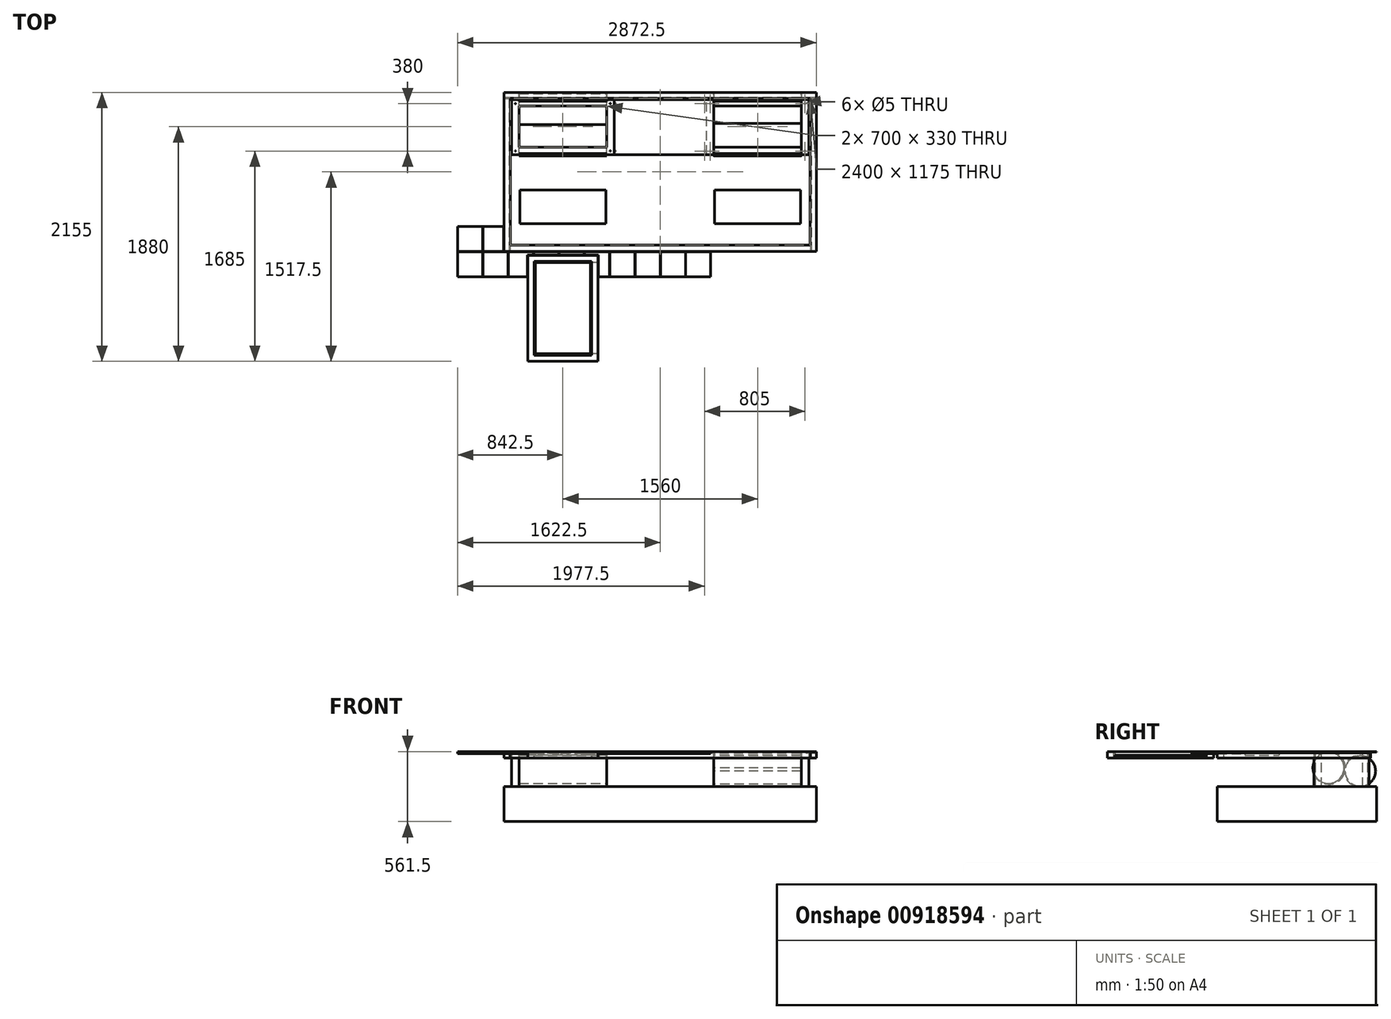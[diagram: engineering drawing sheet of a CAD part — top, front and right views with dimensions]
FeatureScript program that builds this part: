
annotation { "Feature Type Name" : "Feature", "Feature Type Description" : "" }
export const myFeature = defineFeature(function(context is Context, id is Id, definition is map)
    precondition{}
    {
        {
            var Q0;
            Q0=qCreatedBy(makeId("Top.planeOp"),FACE);
            var sketch = newSketch(context, id + "F0", { "sketchPlane" : qUnion([Q0])});
            skLineSegment(sketch, "E0.bottom", {"start": v(-1000, 0) * mm, "end": v(-560, 0) * mm});
            skLineSegment(sketch, "E0.top", {"start": v(-1000, 730) * mm, "end": v(-560, 730) * mm});
            skLineSegment(sketch, "E0.left", {"start": v(-1000, 0) * mm, "end": v(-1000, 730) * mm});
            skLineSegment(sketch, "E0.right", {"start": v(-560, 0) * mm, "end": v(-560, 730) * mm});
            skLineSegment(sketch, "E1.bottom", {"start": v(-1190, 880) * mm, "end": v(1190, 880) * mm});
            skLineSegment(sketch, "E1.top", {"start": v(-1190, 1475) * mm, "end": v(1190, 1475) * mm});
            skLineSegment(sketch, "E1.left", {"start": v(-1190, 880) * mm, "end": v(-1190, 1475) * mm});
            skLineSegment(sketch, "E1.right", {"start": v(1190, 880) * mm, "end": v(1190, 1475) * mm});
            skLineSegment(sketch, "E2.bottom", {"start": v(-1190, 1595) * mm, "end": v(1190, 1595) * mm});
            skLineSegment(sketch, "E2.top", {"start": v(-1190, 2035) * mm, "end": v(1190, 2035) * mm});
            skLineSegment(sketch, "E2.left", {"start": v(-1190, 1595) * mm, "end": v(-1190, 2035) * mm});
            skLineSegment(sketch, "E2.right", {"start": v(1190, 1595) * mm, "end": v(1190, 2035) * mm});
            skLineSegment(sketch, "E3", {"start": v(0, 0) * mm, "end": v(0, 2541.23) * mm, "construction": true});
            skLineSegment(sketch, "E4", {"start": v(-2590, 9087.14) * mm, "end": v(-2590, 297.64) * mm, "construction": true});
            skLineSegment(sketch, "E5", {"start": v(-3236.4, 5035) * mm, "end": v(-2134.23, 5035) * mm, "construction": true});
            skLineSegment(sketch, "E6", {"start": v(-3316.35, 8035) * mm, "end": v(-2134.23, 8035) * mm, "construction": true});
            skLineSegment(sketch, "E7.bottom", {"start": v(-1200, 2045) * mm, "end": v(1200, 2045) * mm});
            skLineSegment(sketch, "E7.top", {"start": v(-1200, 870) * mm, "end": v(1200, 870) * mm});
            skLineSegment(sketch, "E7.left", {"start": v(-1200, 2045) * mm, "end": v(-1200, 870) * mm});
            skLineSegment(sketch, "E7.right", {"start": v(1200, 2045) * mm, "end": v(1200, 870) * mm});
            skLineSegment(sketch, "E8.bottom", {"start": v(-1250, 2095) * mm, "end": v(1250, 2095) * mm});
            skLineSegment(sketch, "E8.top", {"start": v(-1250, 820) * mm, "end": v(1250, 820) * mm});
            skLineSegment(sketch, "E8.left", {"start": v(-1250, 2095) * mm, "end": v(-1250, 820) * mm});
            skLineSegment(sketch, "E8.right", {"start": v(1250, 2095) * mm, "end": v(1250, 820) * mm});
            skLineSegment(sketch, "E9", {"start": v(-780, -123.86) * mm, "end": v(-780, 1756.73) * mm, "construction": true});
            skPoint(sketch, "E9.startSnap0", {"position": v(-780, 0) * mm});
            skLineSegment(sketch, "E10.bottom", {"start": v(-1125, 1314) * mm, "end": v(-435, 1314) * mm});
            skLineSegment(sketch, "E10.top", {"start": v(-1125, 1041) * mm, "end": v(-435, 1041) * mm});
            skLineSegment(sketch, "E10.left", {"start": v(-1125, 1314) * mm, "end": v(-1125, 1041) * mm});
            skLineSegment(sketch, "E10.right", {"start": v(-435, 1314) * mm, "end": v(-435, 1041) * mm});
            skLineSegment(sketch, "E11.MirrorCS", {"start": v(1125, 1041) * mm, "end": v(435, 1041) * mm});
            skLineSegment(sketch, "E12.MirrorCS", {"start": v(435, 1314) * mm, "end": v(435, 1041) * mm});
            skLineSegment(sketch, "E13.MirrorCS", {"start": v(1125, 1314) * mm, "end": v(435, 1314) * mm});
            skLineSegment(sketch, "E14.MirrorCS", {"start": v(1125, 1314) * mm, "end": v(1125, 1041) * mm});
            skSolve(sketch);
        }
        {
            var Q0;
            Q0 = qSketchRegion(id + "F0", true);
            var Q1;
            Q1=makeQuery(id+"F0.imprint","IMPRINT",FACE,{"disambiguationData":[TD([[makeQuery(id+"F0.imprint","IMPRINT",EDGE,{"derivedFrom":sQuery(id+"F0.wireOp",EDGE,"E1.bottom")}),-1.0]])]});
            var Q2;
            Q2=makeQuery(id+"F0.imprint","IMPRINT",FACE,{"disambiguationData":[TD([[makeQuery(id+"F0.imprint","IMPRINT",EDGE,{"derivedFrom":sQuery(id+"F0.wireOp",EDGE,"E2.bottom")}),1.0]])]});
            var Q3;
            Q3=makeQuery(id+"F0.imprint","IMPRINT",FACE,{"disambiguationData":[TD([[makeQuery(id+"F0.imprint","IMPRINT",EDGE,{"derivedFrom":sQuery(id+"F0.wireOp",EDGE,"E10.bottom")}),-1.0]])]});
            var Q4;
            Q4=makeQuery(id+"F0.imprint","IMPRINT",FACE,{"disambiguationData":[TD([[makeQuery(id+"F0.imprint","IMPRINT",EDGE,{"derivedFrom":sQuery(id+"F0.wireOp",EDGE,"E1.bottom")}),1.0]])]});
            var Q5;
            Q5=makeQuery(id+"F0.imprint","IMPRINT",FACE,{"disambiguationData":[TD([[makeQuery(id+"F0.imprint","IMPRINT",EDGE,{"derivedFrom":sQuery(id+"F0.wireOp",EDGE,"E11.MirrorCS")}),-1.0]])]});
            extrude(context, id + "F1", {"entities" : qUnion([Q0, Q1, Q2, Q3, Q4, Q5]), "oppositeDirection" : true, "depth" : 280 * mm, "offsetDistance" : 25 * mm});
        }
        {
            var Q0;
            Q0=makeQuery(id+"F0.imprint","IMPRINT",FACE,{"disambiguationData":[TD([[makeQuery(id+"F0.imprint","IMPRINT",EDGE,{"derivedFrom":sQuery(id+"F0.wireOp",EDGE,"E2.bottom")}),1.0]])]});
            var Q1;
            Q1=makeQuery(id+"F0.imprint","IMPRINT",FACE,{"disambiguationData":[TD([[makeQuery(id+"F0.imprint","IMPRINT",EDGE,{"derivedFrom":sQuery(id+"F0.wireOp",EDGE,"E10.bottom")}),-1.0]])]});
            var Q2;
            Q2=makeQuery(id+"F0.imprint","IMPRINT",FACE,{"disambiguationData":[TD([[makeQuery(id+"F0.imprint","IMPRINT",EDGE,{"derivedFrom":sQuery(id+"F0.wireOp",EDGE,"E11.MirrorCS")}),-1.0]])]});
            var Q3;
            Q3=makeQuery(id+"F0.imprint","IMPRINT",FACE,{"disambiguationData":[TD([[makeQuery(id+"F0.imprint","IMPRINT",EDGE,{"derivedFrom":sQuery(id+"F0.wireOp",EDGE,"E0.bottom")}),1.0]])]});
            var Q4;
            Q4=makeQuery(id+"F0.imprint","IMPRINT",FACE,{"disambiguationData":[TD([[makeQuery(id+"F0.imprint","IMPRINT",EDGE,{"derivedFrom":sQuery(id+"F0.wireOp",EDGE,"E7.bottom")}),1.0]])]});
            extrude(context, id + "F2", {"entities" : qUnion([Q0, Q1, Q2, Q3, Q4]), "depth" : 280 * mm, "offsetDistance" : 25 * mm});
        }
        {
            var Q0;
            Q0=makeQuery(id+"F2.opExtrude","SWEPT_FACE",FACE,{"disambiguationData":[OSD([sQuery(id+"F0.wireOp",EDGE,"E8.top")])]});
            var sketch = newSketch(context, id + "F3", { "sketchPlane" : qUnion([Q0])});
            skLineSegment(sketch, "E15.0.0", {"start": v(-1250, 0) * mm, "end": v(1250, 0) * mm});
            skLineSegment(sketch, "E15.0.1", {"start": v(1250, 0) * mm, "end": v(1250, 280) * mm});
            skLineSegment(sketch, "E15.0.2", {"start": v(1250, 280) * mm, "end": v(-1250, 280) * mm});
            skLineSegment(sketch, "E15.0.3", {"start": v(-1250, 280) * mm, "end": v(-1250, 0) * mm});
            skLineSegment(sketch, "E16", {"start": v(-1204, 271) * mm, "end": v(-1204, 253.4) * mm});
            skLineSegment(sketch, "E17", {"start": v(-1204, 276) * mm, "end": v(-1203.5, 276) * mm});
            skLineSegment(sketch, "E18", {"start": v(-1200, 230) * mm, "end": v(-1200, 0) * mm});
            skLineSegment(sketch, "E19.bottom", {"start": v(-1200, 230) * mm, "end": v(1200, 230) * mm});
            skLineSegment(sketch, "E19.top", {"start": v(-1200, 0) * mm, "end": v(1200, 0) * mm});
            skLineSegment(sketch, "E19.right", {"start": v(1200, 230) * mm, "end": v(1200, 0) * mm});
            skPoint(sketch, "E20.visualSharp", {"position": v(-1204, 276) * mm});
            skArc(sketch, "E20.filletArc", {"start": v(-1204, 271) * mm, "mid": v(-1205.46, 274.54) * mm, "end": v(-1209, 276) * mm});
            skLineSegment(sketch, "E21", {"start": v(-1200, 230) * mm, "end": v(-1200, 280) * mm});
            skLineSegment(sketch, "E22.bottom", {"start": v(-1204, 271) * mm, "end": v(-1200, 271) * mm});
            skLineSegment(sketch, "E22.top", {"start": v(-1203.28, 230) * mm, "end": v(-1200, 230) * mm});
            skLineSegment(sketch, "E22.right", {"start": v(-1200, 271) * mm, "end": v(-1200, 230) * mm});
            skLineSegment(sketch, "E23", {"start": v(-1204, 271) * mm, "end": v(-1203.28, 230) * mm});
            skLineSegment(sketch, "E24", {"start": v(-1203.5, 276) * mm, "end": v(-1204, 276) * mm});
            skLineSegment(sketch, "E25", {"start": v(-1209, 276) * mm, "end": v(-1250, 276.72) * mm});
            skLineSegment(sketch, "E26.MirrorCS", {"start": v(-1209, -276) * mm, "end": v(-1250, -276.72) * mm});
            skLineSegment(sketch, "E27.MirrorCS", {"start": v(-1204, -271) * mm, "end": v(-1203.28, -230) * mm});
            skArc(sketch, "E28.MirrorCS", {"start": v(-1204, -271) * mm, "mid": v(-1205.46, -274.54) * mm, "end": v(-1209, -276) * mm});
            skLineSegment(sketch, "E29", {"start": v(0, 0) * mm, "end": v(0, 422.99) * mm, "construction": true});
            skLineSegment(sketch, "E30.MirrorCS", {"start": v(1203.28, 230) * mm, "end": v(1200, 230) * mm});
            skLineSegment(sketch, "E31.MirrorCS", {"start": v(1209, 276) * mm, "end": v(1250, 276.72) * mm});
            skLineSegment(sketch, "E32.MirrorCS", {"start": v(1204, 271) * mm, "end": v(1203.28, 230) * mm});
            skArc(sketch, "E33.MirrorCS", {"start": v(1204, 271) * mm, "mid": v(1205.46, 274.54) * mm, "end": v(1209, 276) * mm});
            skLineSegment(sketch, "E34.MirrorCS", {"start": v(1200, 230) * mm, "end": v(1200, 280) * mm});
            skLineSegment(sketch, "E35.MirrorCS", {"start": v(1200, 271) * mm, "end": v(1200, 230) * mm});
            skSolve(sketch);
        }
        {
            var Q0;
            {var subQ0=sQuery(id+"F3.wireOp",EDGE,"E19.right");Q0=makeQuery(id+"F3.imprint","IMPRINT",FACE,{"disambiguationData":[TD([[makeQuery(id+"F3.imprint","IMPRINT",EDGE,{"derivedFrom":subQ0}),1.0]])]});}
            var Q1;
            {var subQ0=sQuery(id+"F3.wireOp",EDGE,"E18");Q1=makeQuery(id+"F3.imprint","IMPRINT",FACE,{"disambiguationData":[TD([[makeQuery(id+"F3.imprint","IMPRINT",EDGE,{"derivedFrom":subQ0}),-1.0]])]});}
            extrude(context, id + "F4", {"entities" : qUnion([Q0, Q1]), "operationType" : NewBodyOperationType.REMOVE, "oppositeDirection" : true, "depth" : (1155 + 70) * mm, "offsetDistance" : 25 * mm});
        }
        {
            var Q0;
            Q0=makeQuery(id+"F3.imprint","IMPRINT",FACE,{"disambiguationData":[TD([[makeQuery(id+"F3.imprint","IMPRINT",EDGE,{"derivedFrom":sQuery(id+"F3.wireOp",EDGE,"E19.bottom")}),-1.0]])]});
            extrude(context, id + "F5", {"entities" : qUnion([Q0]), "operationType" : NewBodyOperationType.REMOVE, "oppositeDirection" : true, "depth" : 50 * mm, "offsetDistance" : 25 * mm});
        }
        {
            var Q0;
            Q0=makeQuery(id+"F2.opExtrude","SWEPT_FACE",FACE,{"disambiguationData":[OSD([sQuery(id+"F0.wireOp",EDGE,"E8.right")])]});
            var sketch = newSketch(context, id + "F6", { "sketchPlane" : qUnion([Q0])});
            skLineSegment(sketch, "E36.0.1", {"start": v(820, 276) * mm, "end": v(820, 271) * mm});
            skLineSegment(sketch, "E36.0.2", {"start": v(820, 271) * mm, "end": v(2045, 271) * mm});
            skLineSegment(sketch, "E37.0.0", {"start": v(2095, 230) * mm, "end": v(2095, 271) * mm});
            skLineSegment(sketch, "E37.0.2", {"start": v(820, 271) * mm, "end": v(820, 230) * mm});
            skLineSegment(sketch, "E37.0.3", {"start": v(820, 230) * mm, "end": v(2048.28, 230) * mm});
            skLineSegment(sketch, "E38.0.0", {"start": v(2045, 230) * mm, "end": v(2045, 0) * mm});
            skLineSegment(sketch, "E38.0.1", {"start": v(2045, 0) * mm, "end": v(2095, 0) * mm});
            skLineSegment(sketch, "E38.0.2", {"start": v(2095, 0) * mm, "end": v(2095, 230) * mm});
            skLineSegment(sketch, "E38.0.3", {"start": v(2048.28, 230) * mm, "end": v(2045, 230) * mm});
            skLineSegment(sketch, "E39", {"start": v(2045, 280) * mm, "end": v(2045, 230) * mm});
            skPoint(sketch, "E40.newPointB", {"position": v(820, 276) * mm});
            skArc(sketch, "E40.filletArc", {"start": v(2054, 276) * mm, "mid": v(2050.46, 274.54) * mm, "end": v(2049, 271) * mm});
            skLineSegment(sketch, "E41", {"start": v(2054, 276) * mm, "end": v(2095, 276.72) * mm});
            skLineSegment(sketch, "E42", {"start": v(2049, 271) * mm, "end": v(2048.28, 230) * mm});
            skLineSegment(sketch, "E43", {"start": v(2095, 280) * mm, "end": v(2095, 276.72) * mm});
            skLineSegment(sketch, "E44.trimOffspring", {"start": v(2045, 271) * mm, "end": v(820, 271) * mm});
            skLineSegment(sketch, "E45", {"start": v(2045, 280) * mm, "end": v(2095, 280) * mm});
            skLineSegment(sketch, "E46", {"start": v(2045, 230) * mm, "end": v(2048.28, 230) * mm});
            skSolve(sketch);
        }
        {
            var Q0;
            {var subQ0=sQuery(id+"F6.wireOp",EDGE,"E37.0.0");Q0=makeQuery(id+"F6.imprint","IMPRINT",FACE,{"disambiguationData":[TD([[makeQuery(id+"F6.imprint","IMPRINT",EDGE,{"derivedFrom":subQ0}),-1.0]])]});}
            extrude(context, id + "F7", {"entities" : qUnion([Q0]), "operationType" : NewBodyOperationType.REMOVE, "oppositeDirection" : true, "depth" : 2500 * mm, "offsetDistance" : 25 * mm});
        }
        {
            var Q0;
            Q0=makeQuery(id+"F2.opExtrude","CAP_FACE",FACE,{"disambiguationData":[OSD([sQuery(id+"F0.wireOp",EDGE,"E2.bottom"),sQuery(id+"F0.wireOp",EDGE,"E2.top"),sQuery(id+"F0.wireOp",EDGE,"E2.left"),sQuery(id+"F0.wireOp",EDGE,"E2.right")])],"isStart":false});
            var sketch = newSketch(context, id + "F8", { "sketchPlane" : qUnion([Q0])});
            skLineSegment(sketch, "E47.0.0", {"start": v(-1250, 2095) * mm, "end": v(-1250, 820) * mm});
            skLineSegment(sketch, "E47.0.1", {"start": v(-1250, 820) * mm, "end": v(1250, 820) * mm});
            skLineSegment(sketch, "E47.0.2", {"start": v(1250, 820) * mm, "end": v(1250, 2095) * mm});
            skLineSegment(sketch, "E47.0.3", {"start": v(1250, 2095) * mm, "end": v(-1250, 2095) * mm});
            skLineSegment(sketch, "E48.0.0", {"start": v(-560, 730) * mm, "end": v(-1000, 730) * mm});
            skLineSegment(sketch, "E48.0.1", {"start": v(-1000, 730) * mm, "end": v(-1000, 0) * mm});
            skLineSegment(sketch, "E48.0.2", {"start": v(-1000, 0) * mm, "end": v(-560, 0) * mm});
            skLineSegment(sketch, "E48.0.3", {"start": v(-560, 0) * mm, "end": v(-560, 730) * mm});
            skLineSegment(sketch, "E49", {"start": v(0, 2970.73) * mm, "end": v(0, -1424.68) * mm, "construction": true});
            skPoint(sketch, "E49.endSnap0", {"position": v(0, 2095) * mm});
            skLineSegment(sketch, "E50.bottom", {"start": v(1.5, 817) * mm, "end": v(201.5, 817) * mm});
            skLineSegment(sketch, "E50.top", {"start": v(1.5, 617) * mm, "end": v(201.5, 617) * mm});
            skLineSegment(sketch, "E50.left", {"start": v(1.5, 817) * mm, "end": v(1.5, 617) * mm});
            skLineSegment(sketch, "E50.right", {"start": v(201.5, 817) * mm, "end": v(201.5, 617) * mm});
            skLineSegment(sketch, "E51.bottom", {"start": v(204.5, 817) * mm, "end": v(404.5, 817) * mm});
            skLineSegment(sketch, "E51.top", {"start": v(204.5, 617) * mm, "end": v(404.5, 617) * mm});
            skLineSegment(sketch, "E51.left", {"start": v(204.5, 817) * mm, "end": v(204.5, 617) * mm});
            skLineSegment(sketch, "E51.right", {"start": v(404.5, 817) * mm, "end": v(404.5, 617) * mm});
            skLineSegment(sketch, "E52.bottom", {"start": v(-1.5, 817) * mm, "end": v(-201.5, 817) * mm});
            skLineSegment(sketch, "E52.top", {"start": v(-1.5, 617) * mm, "end": v(-201.5, 617) * mm});
            skLineSegment(sketch, "E52.left", {"start": v(-1.5, 817) * mm, "end": v(-1.5, 617) * mm});
            skLineSegment(sketch, "E52.right", {"start": v(-201.5, 817) * mm, "end": v(-201.5, 617) * mm});
            skLineSegment(sketch, "E53.bottom", {"start": v(-204.5, 817) * mm, "end": v(-404.5, 817) * mm});
            skLineSegment(sketch, "E53.top", {"start": v(-204.5, 617) * mm, "end": v(-404.5, 617) * mm});
            skLineSegment(sketch, "E53.left", {"start": v(-204.5, 817) * mm, "end": v(-204.5, 617) * mm});
            skLineSegment(sketch, "E53.right", {"start": v(-404.5, 817) * mm, "end": v(-404.5, 617) * mm});
            skLineSegment(sketch, "E54.bottom", {"start": v(-407.5, 817) * mm, "end": v(-607.5, 817) * mm});
            skLineSegment(sketch, "E54.top", {"start": v(-407.5, 617) * mm, "end": v(-497, 617) * mm});
            skLineSegment(sketch, "E54.left", {"start": v(-407.5, 817) * mm, "end": v(-407.5, 617) * mm});
            skLineSegment(sketch, "E54.right", {"start": v(-607.5, 817) * mm, "end": v(-607.5, 793) * mm});
            skLineSegment(sketch, "E55.bottom", {"start": v(-1060, 790) * mm, "end": v(-500, 790) * mm});
            skLineSegment(sketch, "E55.top", {"start": v(-1010, 740) * mm, "end": v(-607.5, 740) * mm});
            skLineSegment(sketch, "E55.left", {"start": v(-1060, 790) * mm, "end": v(-1060, 740) * mm});
            skLineSegment(sketch, "E55.right", {"start": v(-500, 790) * mm, "end": v(-500, 740) * mm});
            skLineSegment(sketch, "E56.bottom", {"start": v(-1060, 790) * mm, "end": v(-1010, 790) * mm});
            skLineSegment(sketch, "E56.left", {"start": v(-1060, 790) * mm, "end": v(-1060, -60) * mm});
            skLineSegment(sketch, "E56.right", {"start": v(-1010, 740) * mm, "end": v(-1010, -10) * mm});
            skLineSegment(sketch, "E57.bottom", {"start": v(-500, 790) * mm, "end": v(-550, 790) * mm});
            skLineSegment(sketch, "E57.top", {"start": v(-500, -60) * mm, "end": v(-550, -60) * mm});
            skLineSegment(sketch, "E57.left", {"start": v(-500, 790) * mm, "end": v(-500, -60) * mm});
            skLineSegment(sketch, "E57.right", {"start": v(-550, 740) * mm, "end": v(-550, -10) * mm});
            skLineSegment(sketch, "E58.bottom", {"start": v(-500, -60) * mm, "end": v(-1060, -60) * mm});
            skLineSegment(sketch, "E58.top", {"start": v(-550, -10) * mm, "end": v(-1010, -10) * mm});
            skLineSegment(sketch, "E58.left", {"start": v(-500, -60) * mm, "end": v(-500, -10) * mm});
            skLineSegment(sketch, "E58.right", {"start": v(-1060, -60) * mm, "end": v(-1060, -10) * mm});
            skLineSegment(sketch, "E59", {"start": v(-607.5, 740) * mm, "end": v(-550, 740) * mm});
            skLineSegment(sketch, "E60", {"start": v(-607.5, 793) * mm, "end": v(-497, 793) * mm});
            skLineSegment(sketch, "E61", {"start": v(-497, 793) * mm, "end": v(-497, 617) * mm});
            skPoint(sketch, "E62.orphan", {"position": v(-607.5, 617) * mm});
            skLineSegment(sketch, "E63.bottom", {"start": v(-610.5, 817) * mm, "end": v(-810.5, 817) * mm});
            skLineSegment(sketch, "E63.top", {"start": v(-610.5, 793) * mm, "end": v(-810.5, 793) * mm});
            skLineSegment(sketch, "E63.left", {"start": v(-610.5, 817) * mm, "end": v(-610.5, 793) * mm});
            skLineSegment(sketch, "E63.right", {"start": v(-810.5, 817) * mm, "end": v(-810.5, 793) * mm});
            skLineSegment(sketch, "E64.bottom", {"start": v(-813.5, 817) * mm, "end": v(-1013.5, 817) * mm});
            skLineSegment(sketch, "E64.top", {"start": v(-813.5, 793) * mm, "end": v(-1013.5, 793) * mm});
            skLineSegment(sketch, "E64.left", {"start": v(-813.5, 817) * mm, "end": v(-813.5, 793) * mm});
            skLineSegment(sketch, "E64.right", {"start": v(-1013.5, 817) * mm, "end": v(-1013.5, 793) * mm});
            skLineSegment(sketch, "E65.bottom", {"start": v(-1016.5, 817) * mm, "end": v(-1216.5, 817) * mm});
            skLineSegment(sketch, "E65.left", {"start": v(-1016.5, 817) * mm, "end": v(-1016.5, 793) * mm});
            skLineSegment(sketch, "E65.right", {"start": v(-1216.5, 817) * mm, "end": v(-1216.5, 617) * mm});
            skLineSegment(sketch, "E66", {"start": v(-1016.5, 793) * mm, "end": v(-1063, 793) * mm});
            skLineSegment(sketch, "E67", {"start": v(-1063, 793) * mm, "end": v(-1063, 617) * mm});
            skLineSegment(sketch, "E68.trimOffspring", {"start": v(-1063, 617) * mm, "end": v(-1216.5, 617) * mm});
            skLineSegment(sketch, "E69.bottom", {"start": v(-1219.5, 817) * mm, "end": v(-1419.5, 817) * mm});
            skLineSegment(sketch, "E69.top", {"start": v(-1219.5, 617) * mm, "end": v(-1419.5, 617) * mm});
            skLineSegment(sketch, "E69.left", {"start": v(-1219.5, 817) * mm, "end": v(-1219.5, 617) * mm});
            skLineSegment(sketch, "E69.right", {"start": v(-1419.5, 817) * mm, "end": v(-1419.5, 617) * mm});
            skLineSegment(sketch, "E70.bottom", {"start": v(-1422.5, 817) * mm, "end": v(-1622.5, 817) * mm});
            skLineSegment(sketch, "E70.top", {"start": v(-1422.5, 617) * mm, "end": v(-1622.5, 617) * mm});
            skLineSegment(sketch, "E70.left", {"start": v(-1422.5, 817) * mm, "end": v(-1422.5, 617) * mm});
            skLineSegment(sketch, "E70.right", {"start": v(-1622.5, 817) * mm, "end": v(-1622.5, 617) * mm});
            skLineSegment(sketch, "E71.bottom", {"start": v(-1622.5, 820) * mm, "end": v(-1422.5, 820) * mm});
            skLineSegment(sketch, "E71.top", {"start": v(-1622.5, 1020) * mm, "end": v(-1422.5, 1020) * mm});
            skLineSegment(sketch, "E71.left", {"start": v(-1622.5, 820) * mm, "end": v(-1622.5, 1020) * mm});
            skLineSegment(sketch, "E71.right", {"start": v(-1422.5, 820) * mm, "end": v(-1422.5, 1020) * mm});
            skLineSegment(sketch, "E72.bottom", {"start": v(-1419.5, 820) * mm, "end": v(-1253, 820) * mm});
            skLineSegment(sketch, "E72.top", {"start": v(-1419.5, 1020) * mm, "end": v(-1253, 1020) * mm});
            skLineSegment(sketch, "E72.left", {"start": v(-1419.5, 820) * mm, "end": v(-1419.5, 1020) * mm});
            skLineSegment(sketch, "E72.right", {"start": v(-1253, 820) * mm, "end": v(-1253, 1020) * mm});
            skSolve(sketch);
        }
        {
            var Q0;
            Q0=makeQuery(id+"F8.imprint","IMPRINT",FACE,{"disambiguationData":[TD([[makeQuery(id+"F8.imprint","IMPRINT",EDGE,{"derivedFrom":sQuery(id+"F8.wireOp",EDGE,"E71.bottom")}),1.0]])]});
            var Q1;
            Q1=makeQuery(id+"F8.imprint","IMPRINT",FACE,{"disambiguationData":[TD([[makeQuery(id+"F8.imprint","IMPRINT",EDGE,{"derivedFrom":sQuery(id+"F8.wireOp",EDGE,"E72.bottom")}),1.0]])]});
            var Q2;
            Q2=makeQuery(id+"F8.imprint","IMPRINT",FACE,{"disambiguationData":[TD([[makeQuery(id+"F8.imprint","IMPRINT",EDGE,{"derivedFrom":sQuery(id+"F8.wireOp",EDGE,"E70.bottom")}),1.0]])]});
            var Q3;
            Q3=makeQuery(id+"F8.imprint","IMPRINT",FACE,{"disambiguationData":[TD([[makeQuery(id+"F8.imprint","IMPRINT",EDGE,{"derivedFrom":sQuery(id+"F8.wireOp",EDGE,"E69.bottom")}),1.0]])]});
            var Q4;
            Q4=makeQuery(id+"F8.imprint","IMPRINT",FACE,{"disambiguationData":[TD([[makeQuery(id+"F8.imprint","IMPRINT",EDGE,{"derivedFrom":sQuery(id+"F8.wireOp",EDGE,"E65.bottom")}),1.0]])]});
            var Q5;
            Q5=makeQuery(id+"F8.imprint","IMPRINT",FACE,{"disambiguationData":[TD([[makeQuery(id+"F8.imprint","IMPRINT",EDGE,{"derivedFrom":sQuery(id+"F8.wireOp",EDGE,"E64.bottom")}),1.0]])]});
            var Q6;
            Q6=makeQuery(id+"F8.imprint","IMPRINT",FACE,{"disambiguationData":[TD([[makeQuery(id+"F8.imprint","IMPRINT",EDGE,{"derivedFrom":sQuery(id+"F8.wireOp",EDGE,"E63.bottom")}),1.0]])]});
            var Q7;
            Q7=makeQuery(id+"F8.imprint","IMPRINT",FACE,{"disambiguationData":[TD([[makeQuery(id+"F8.imprint","IMPRINT",EDGE,{"derivedFrom":sQuery(id+"F8.wireOp",EDGE,"E54.bottom")}),1.0]])]});
            var Q8;
            Q8=makeQuery(id+"F8.imprint","IMPRINT",FACE,{"disambiguationData":[TD([[makeQuery(id+"F8.imprint","IMPRINT",EDGE,{"derivedFrom":sQuery(id+"F8.wireOp",EDGE,"E53.bottom")}),1.0]])]});
            var Q9;
            Q9=makeQuery(id+"F8.imprint","IMPRINT",FACE,{"disambiguationData":[TD([[makeQuery(id+"F8.imprint","IMPRINT",EDGE,{"derivedFrom":sQuery(id+"F8.wireOp",EDGE,"E52.bottom")}),1.0]])]});
            var Q10;
            Q10=makeQuery(id+"F8.imprint","IMPRINT",FACE,{"disambiguationData":[TD([[makeQuery(id+"F8.imprint","IMPRINT",EDGE,{"derivedFrom":sQuery(id+"F8.wireOp",EDGE,"E50.bottom")}),-1.0]])]});
            var Q11;
            Q11=makeQuery(id+"F8.imprint","IMPRINT",FACE,{"disambiguationData":[TD([[makeQuery(id+"F8.imprint","IMPRINT",EDGE,{"derivedFrom":sQuery(id+"F8.wireOp",EDGE,"E51.bottom")}),-1.0]])]});
            extrude(context, id + "F9", {"entities" : qUnion([Q0, Q1, Q2, Q3, Q4, Q5, Q6, Q7, Q8, Q9, Q10, Q11]), "oppositeDirection" : true, "depth" : 16 * mm, "offsetDistance" : 25 * mm});
        }
        {
            var Q0;
            Q0=makeQuery(id+"F8.imprint","IMPRINT",FACE,{"disambiguationData":[TD([[makeQuery(id+"F8.imprint","IMPRINT",EDGE,{"derivedFrom":sQuery(id+"F8.wireOp",EDGE,"E55.bottom")}),-1.0]])]});
            extrude(context, id + "F10", {"entities" : qUnion([Q0]), "oppositeDirection" : true, "depth" : 50 * mm, "offsetDistance" : 25 * mm});
        }
        {
            var Q0;
            Q0=makeQuery(id+"F2.opExtrude","CAP_FACE",FACE,{"disambiguationData":[OSD([sQuery(id+"F0.wireOp",EDGE,"E2.bottom"),sQuery(id+"F0.wireOp",EDGE,"E2.top"),sQuery(id+"F0.wireOp",EDGE,"E2.left"),sQuery(id+"F0.wireOp",EDGE,"E2.right")])],"isStart":false});
            var sketch = newSketch(context, id + "F11", { "sketchPlane" : qUnion([Q0])});
            skLineSegment(sketch, "E73.0.0", {"start": v(1190, 2035) * mm, "end": v(-1190, 2035) * mm});
            skLineSegment(sketch, "E73.0.1", {"start": v(-1190, 2035) * mm, "end": v(-1190, 1595) * mm});
            skLineSegment(sketch, "E73.0.2", {"start": v(-1190, 1595) * mm, "end": v(1190, 1595) * mm});
            skLineSegment(sketch, "E73.0.3", {"start": v(1190, 1595) * mm, "end": v(1190, 2035) * mm});
            skLineSegment(sketch, "E74", {"start": v(0, 2342.29) * mm, "end": v(0, 307.7) * mm, "construction": true});
            skLineSegment(sketch, "E75.bottom", {"start": v(-1190, 2035) * mm, "end": v(-1130, 2035) * mm});
            skLineSegment(sketch, "E75.top", {"start": v(-1190, 1595) * mm, "end": v(-1130, 1595) * mm});
            skLineSegment(sketch, "E75.right", {"start": v(-1130, 2035) * mm, "end": v(-1130, 1595) * mm});
            skLineSegment(sketch, "E76.bottom", {"start": v(-1130, 1655) * mm, "end": v(-430, 1655) * mm});
            skLineSegment(sketch, "E76.top", {"start": v(-1130, 1605) * mm, "end": v(-430, 1605) * mm});
            skLineSegment(sketch, "E76.left", {"start": v(-1130, 1655) * mm, "end": v(-1130, 1605) * mm});
            skLineSegment(sketch, "E76.right", {"start": v(-430, 1655) * mm, "end": v(-430, 1605) * mm});
            skLineSegment(sketch, "E77.bottom", {"start": v(-430, 1595) * mm, "end": v(-370, 1595) * mm});
            skLineSegment(sketch, "E77.top", {"start": v(-430, 2035) * mm, "end": v(-370, 2035) * mm});
            skLineSegment(sketch, "E77.left", {"start": v(-430, 1595) * mm, "end": v(-430, 2035) * mm});
            skLineSegment(sketch, "E77.right", {"start": v(-370, 1595) * mm, "end": v(-370, 2035) * mm});
            skLineSegment(sketch, "E78.bottom", {"start": v(-1130, 2025) * mm, "end": v(-430, 2025) * mm});
            skLineSegment(sketch, "E78.top", {"start": v(-1130, 1985) * mm, "end": v(-430, 1985) * mm});
            skLineSegment(sketch, "E78.left", {"start": v(-1130, 2025) * mm, "end": v(-1130, 1985) * mm});
            skLineSegment(sketch, "E78.right", {"start": v(-430, 2025) * mm, "end": v(-430, 1985) * mm});
            skLineSegment(sketch, "E79.MirrorCS", {"start": v(1130, 2025) * mm, "end": v(430, 2025) * mm});
            skLineSegment(sketch, "E80.MirrorCS", {"start": v(1130, 2035) * mm, "end": v(1130, 1595) * mm});
            skLineSegment(sketch, "E81.MirrorCS", {"start": v(1190, 2035) * mm, "end": v(1190, 1595) * mm});
            skLineSegment(sketch, "E82.MirrorCS", {"start": v(1130, 1985) * mm, "end": v(430, 1985) * mm});
            skLineSegment(sketch, "E83.MirrorCS", {"start": v(430, 1595) * mm, "end": v(430, 2035) * mm});
            skLineSegment(sketch, "E84.MirrorCS", {"start": v(370, 1595) * mm, "end": v(370, 2035) * mm});
            skLineSegment(sketch, "E85.MirrorCS", {"start": v(1130, 1605) * mm, "end": v(430, 1605) * mm});
            skLineSegment(sketch, "E86.MirrorCS", {"start": v(1130, 1655) * mm, "end": v(430, 1655) * mm});
            skLineSegment(sketch, "E87", {"start": v(-1285.78, 2005) * mm, "end": v(1392.46, 2005) * mm, "construction": true});
            skPoint(sketch, "E87.startSnap0", {"position": v(-1130, 2005) * mm});
            skLineSegment(sketch, "E88", {"start": v(-1296.18, 1625) * mm, "end": v(1385.26, 1625) * mm, "construction": true});
            skLineSegment(sketch, "E89", {"start": v(-400, 2119.83) * mm, "end": v(-400, 1542.7) * mm, "construction": true});
            skLineSegment(sketch, "E90", {"start": v(-1160, 2117.02) * mm, "end": v(-1160, 1527.48) * mm, "construction": true});
            skPoint(sketch, "E90.startSnap0", {"position": v(-1160, 2035) * mm});
            skCircle(sketch, "E91", {"center": v(-1160, 2005) * mm, "radius": 2.5 * mm});
            skCircle(sketch, "E92", {"center": v(-1160, 1625) * mm, "radius": 2.5 * mm});
            skCircle(sketch, "E93", {"center": v(-400, 2005) * mm, "radius": 2.5 * mm});
            skCircle(sketch, "E94", {"center": v(-400, 1625) * mm, "radius": 2.5 * mm});
            skLineSegment(sketch, "E95", {"start": v(-355, 2206.01) * mm, "end": v(-355, 1556.36) * mm, "construction": true});
            skCircle(sketch, "E96", {"center": v(-355, 2005) * mm, "radius": 2.5 * mm});
            skCircle(sketch, "E97", {"center": v(-355, 1625) * mm, "radius": 2.5 * mm});
            skCircle(sketch, "E98.MirrorC", {"center": v(355, 2005) * mm, "radius": 2.5 * mm});
            skCircle(sketch, "E99.MirrorC", {"center": v(400, 2005) * mm, "radius": 2.5 * mm});
            skCircle(sketch, "E100.MirrorC", {"center": v(355, 1625) * mm, "radius": 2.5 * mm});
            skCircle(sketch, "E101.MirrorC", {"center": v(400, 1625) * mm, "radius": 2.5 * mm});
            skCircle(sketch, "E102.MirrorC", {"center": v(1160, 1625) * mm, "radius": 2.5 * mm});
            skCircle(sketch, "E103.MirrorC", {"center": v(1160, 2005) * mm, "radius": 2.5 * mm});
            skSolve(sketch);
        }
        {
            var Q0;
            Q0=makeQuery(id+"F11.imprint","IMPRINT",FACE,{"disambiguationData":[TD([[makeQuery(id+"F11.imprint","IMPRINT",EDGE,{"derivedFrom":sQuery(id+"F11.wireOp",EDGE,"E98.MirrorC")}),-1.0]])]});
            var Q1;
            Q1=makeQuery(id+"F11.imprint","IMPRINT",FACE,{"disambiguationData":[TD([[makeQuery(id+"F11.imprint","IMPRINT",EDGE,{"derivedFrom":sQuery(id+"F11.wireOp",EDGE,"E99.MirrorC")}),-1.0]])]});
            var Q2;
            Q2=makeQuery(id+"F11.imprint","IMPRINT",FACE,{"disambiguationData":[TD([[makeQuery(id+"F11.imprint","IMPRINT",EDGE,{"derivedFrom":sQuery(id+"F11.wireOp",EDGE,"E100.MirrorC")}),-1.0]])]});
            var Q3;
            Q3=makeQuery(id+"F11.imprint","IMPRINT",FACE,{"disambiguationData":[TD([[makeQuery(id+"F11.imprint","IMPRINT",EDGE,{"derivedFrom":sQuery(id+"F11.wireOp",EDGE,"E101.MirrorC")}),-1.0]])]});
            var Q4;
            Q4=makeQuery(id+"F11.imprint","IMPRINT",FACE,{"disambiguationData":[TD([[makeQuery(id+"F11.imprint","IMPRINT",EDGE,{"derivedFrom":sQuery(id+"F11.wireOp",EDGE,"E102.MirrorC")}),-1.0]])]});
            var Q5;
            Q5=makeQuery(id+"F11.imprint","IMPRINT",FACE,{"disambiguationData":[TD([[makeQuery(id+"F11.imprint","IMPRINT",EDGE,{"derivedFrom":sQuery(id+"F11.wireOp",EDGE,"E103.MirrorC")}),-1.0]])]});
            var Q6;
            Q6=makeQuery(id+"F11.imprint","IMPRINT",FACE,{"disambiguationData":[TD([[makeQuery(id+"F11.imprint","IMPRINT",EDGE,{"derivedFrom":sQuery(id+"F11.wireOp",EDGE,"E93")}),1.0]])]});
            var Q7;
            Q7=makeQuery(id+"F11.imprint","IMPRINT",FACE,{"disambiguationData":[TD([[makeQuery(id+"F11.imprint","IMPRINT",EDGE,{"derivedFrom":sQuery(id+"F11.wireOp",EDGE,"E96")}),1.0]])]});
            var Q8;
            Q8=makeQuery(id+"F11.imprint","IMPRINT",FACE,{"disambiguationData":[TD([[makeQuery(id+"F11.imprint","IMPRINT",EDGE,{"derivedFrom":sQuery(id+"F11.wireOp",EDGE,"E97")}),1.0]])]});
            var Q9;
            Q9=makeQuery(id+"F11.imprint","IMPRINT",FACE,{"disambiguationData":[TD([[makeQuery(id+"F11.imprint","IMPRINT",EDGE,{"derivedFrom":sQuery(id+"F11.wireOp",EDGE,"E94")}),1.0]])]});
            var Q10;
            Q10=makeQuery(id+"F11.imprint","IMPRINT",FACE,{"disambiguationData":[TD([[makeQuery(id+"F11.imprint","IMPRINT",EDGE,{"derivedFrom":sQuery(id+"F11.wireOp",EDGE,"E91")}),1.0]])]});
            var Q11;
            Q11=makeQuery(id+"F11.imprint","IMPRINT",FACE,{"disambiguationData":[TD([[makeQuery(id+"F11.imprint","IMPRINT",EDGE,{"derivedFrom":sQuery(id+"F11.wireOp",EDGE,"E92")}),1.0]])]});
            extrude(context, id + "F12", {"entities" : qUnion([Q0, Q1, Q2, Q3, Q4, Q5, Q6, Q7, Q8, Q9, Q10, Q11]), "depth" : 1.5 * mm, "offsetDistance" : 25 * mm});
        }
        {
            var Q0;
            {var subQ0=sQuery(id+"F11.wireOp",EDGE,"E76.bottom");Q0=makeQuery(id+"F11.imprint","IMPRINT",FACE,{"disambiguationData":[TD([[makeQuery(id+"F11.imprint","IMPRINT",EDGE,{"derivedFrom":subQ0}),1.0]])]});}
            var Q1;
            {var subQ5=sQuery(id+"F11.wireOp",EDGE,"E76.top");Q1=makeQuery(id+"F11.imprint","IMPRINT",FACE,{"disambiguationData":[TD([[makeQuery(id+"F11.imprint","IMPRINT",EDGE,{"derivedFrom":subQ5}),-1.0]])]});}
            var Q2;
            {var subQ5=sQuery(id+"F11.wireOp",EDGE,"E78.bottom");Q2=makeQuery(id+"F11.imprint","IMPRINT",FACE,{"disambiguationData":[TD([[makeQuery(id+"F11.imprint","IMPRINT",EDGE,{"derivedFrom":subQ5}),1.0]])]});}
            var Q3;
            {var subQ5=sQuery(id+"F11.wireOp",EDGE,"E79.MirrorCS");Q3=makeQuery(id+"F11.imprint","IMPRINT",FACE,{"disambiguationData":[TD([[makeQuery(id+"F11.imprint","IMPRINT",EDGE,{"derivedFrom":subQ5}),-1.0]])]});}
            var Q4;
            {var subQ5=sQuery(id+"F11.wireOp",EDGE,"E85.MirrorCS");Q4=makeQuery(id+"F11.imprint","IMPRINT",FACE,{"disambiguationData":[TD([[makeQuery(id+"F11.imprint","IMPRINT",EDGE,{"derivedFrom":subQ5}),1.0]])]});}
            var Q5;
            {var subQ0=sQuery(id+"F11.wireOp",EDGE,"E82.MirrorCS");Q5=makeQuery(id+"F11.imprint","IMPRINT",FACE,{"disambiguationData":[TD([[makeQuery(id+"F11.imprint","IMPRINT",EDGE,{"derivedFrom":subQ0}),1.0]])]});}
            extrude(context, id + "F13", {"entities" : qUnion([Q0, Q1, Q2, Q3, Q4, Q5]), "operationType" : NewBodyOperationType.REMOVE, "oppositeDirection" : true, "depth" : 280 * mm, "offsetDistance" : 25 * mm});
        }
        {
            var Q0;
            {var subQ0=sQuery(id+"F11.wireOp",EDGE,"E77.left");Q0=makeQuery(id+"F13.boolean.opBoolean","COPY",FACE,{"derivedFrom":makeQuery(id+"F13.opExtrude","SWEPT_FACE",FACE,{"disambiguationData":[OSD([subQ0]),TDD([makeQuery(id+"F11.imprint","IMPRINT",EDGE,{"disambiguationData":[TD([[makeQuery(id+"F11.imprint","INTERSECT",VERTEX,{"derivedFrom":[sQuery(id+"F11.wireOp",EDGE,"E76.bottom"),subQ0]}),-1.0]])],"derivedFrom":subQ0})])]})});}
            var sketch = newSketch(context, id + "F14", { "sketchPlane" : qUnion([Q0])});
            skLineSegment(sketch, "E104", {"start": v(-2040.86, 125.33) * mm, "end": v(-1705.76, 125.33) * mm, "construction": true});
            skLineSegment(sketch, "E105", {"start": v(-1960, 29.8) * mm, "end": v(-1960, 270.8) * mm, "construction": true});
            skLineSegment(sketch, "E106", {"start": v(-1710, 22.85) * mm, "end": v(-1710, 291.74) * mm, "construction": true});
            skLineSegment(sketch, "E107", {"start": v(-1938.23, 150.33) * mm, "end": v(-1724.02, 150.33) * mm, "construction": true});
            skLineSegment(sketch, "E108.0", {"start": v(-1655, 0) * mm, "end": v(-1655, 280) * mm});
            skCircle(sketch, "E109", {"center": v(-1710, 150.33) * mm, "radius": 125 * mm});
            skCircle(sketch, "E110", {"center": v(-1960, 125.33) * mm, "radius": 125 * mm});
            skPoint(sketch, "E111.center.orphan", {"position": v(-1710, 157.3) * mm});
            skSolve(sketch);
        }
        {
            var Q0;
            Q0 = qSketchRegion(id + "F14", true);
            extrude(context, id + "F15", {"entities" : qUnion([Q0]), "depth" : 700 * mm, "offsetDistance" : 25 * mm});
        }
        {
            var Q0;
            {var subQ0=sQuery(id+"F11.wireOp",EDGE,"E83.MirrorCS");Q0=makeQuery(id+"F13.boolean.opBoolean","COPY",FACE,{"derivedFrom":makeQuery(id+"F13.opExtrude","SWEPT_FACE",FACE,{"disambiguationData":[OSD([subQ0]),TDD([makeQuery(id+"F11.imprint","IMPRINT",EDGE,{"disambiguationData":[TD([[makeQuery(id+"F11.imprint","INTERSECT",VERTEX,{"derivedFrom":[sQuery(id+"F11.wireOp",EDGE,"E82.MirrorCS"),subQ0]}),1.0]])],"derivedFrom":subQ0})])]})});}
            var sketch = newSketch(context, id + "F16", { "sketchPlane" : qUnion([Q0])});
            skLineSegment(sketch, "E112", {"start": v(1715, 897.44) * mm, "end": v(1715, 27.74) * mm, "construction": true});
            skLineSegment(sketch, "E113", {"start": v(1965, 869.68) * mm, "end": v(1965, 0) * mm, "construction": true});
            skLineSegment(sketch, "E114", {"start": v(1689.09, 150) * mm, "end": v(2007.15, 150) * mm, "construction": true});
            skCircle(sketch, "E115", {"center": v(1715, 150) * mm, "radius": 130 * mm});
            skLineSegment(sketch, "E116", {"start": v(1861.95, 125) * mm, "end": v(2192.79, 125) * mm, "construction": true});
            skCircle(sketch, "E117", {"center": v(1965, 125) * mm, "radius": 122.5 * mm});
            skSolve(sketch);
        }
        {
            var Q0;
            Q0 = qSketchRegion(id + "F16", true);
            extrude(context, id + "F17", {"entities" : qUnion([Q0]), "depth" : 700 * mm, "offsetDistance" : 25 * mm});
        }
        {
            var Q0;
            Q0=makeQuery(id+"F12.opExtrude","CAP_EDGE",EDGE,{"disambiguationData":[OSD([sQuery(id+"F11.wireOp",EDGE,"E93")])],"isStart":false});
            var Q1;
            Q1=makeQuery(id+"F12.opExtrude","CAP_EDGE",EDGE,{"disambiguationData":[OSD([sQuery(id+"F11.wireOp",EDGE,"E96")])],"isStart":false});
            var Q2;
            Q2=makeQuery(id+"F12.opExtrude","CAP_EDGE",EDGE,{"disambiguationData":[OSD([sQuery(id+"F11.wireOp",EDGE,"E94")])],"isStart":false});
            var Q3;
            Q3=makeQuery(id+"F12.opExtrude","CAP_EDGE",EDGE,{"disambiguationData":[OSD([sQuery(id+"F11.wireOp",EDGE,"E97")])],"isStart":false});
            var Q4;
            Q4=makeQuery(id+"F12.opExtrude","CAP_EDGE",EDGE,{"disambiguationData":[OSD([sQuery(id+"F11.wireOp",EDGE,"E98.MirrorC")])],"isStart":false});
            var Q5;
            Q5=makeQuery(id+"F12.opExtrude","CAP_EDGE",EDGE,{"disambiguationData":[OSD([sQuery(id+"F11.wireOp",EDGE,"E99.MirrorC")])],"isStart":false});
            var Q6;
            Q6=makeQuery(id+"F12.opExtrude","CAP_EDGE",EDGE,{"disambiguationData":[OSD([sQuery(id+"F11.wireOp",EDGE,"E100.MirrorC")])],"isStart":false});
            var Q7;
            Q7=makeQuery(id+"F12.opExtrude","CAP_EDGE",EDGE,{"disambiguationData":[OSD([sQuery(id+"F11.wireOp",EDGE,"E101.MirrorC")])],"isStart":false});
            var Q8;
            Q8=makeQuery(id+"F12.opExtrude","CAP_EDGE",EDGE,{"disambiguationData":[OSD([sQuery(id+"F11.wireOp",EDGE,"E102.MirrorC")])],"isStart":false});
            var Q9;
            Q9=makeQuery(id+"F12.opExtrude","CAP_EDGE",EDGE,{"disambiguationData":[OSD([sQuery(id+"F11.wireOp",EDGE,"E103.MirrorC")])],"isStart":false});
            var Q10;
            Q10=makeQuery(id+"F12.opExtrude","CAP_FACE",FACE,{"disambiguationData":[OSD([sQuery(id+"F11.wireOp",EDGE,"E91")])],"isStart":false});
            var Q11;
            Q11=makeQuery(id+"F12.opExtrude","CAP_EDGE",EDGE,{"disambiguationData":[OSD([sQuery(id+"F11.wireOp",EDGE,"E92")])],"isStart":false});
            fillet(context, id + "F18", {"entities" : qUnion([Q0, Q1, Q2, Q3, Q4, Q5, Q6, Q7, Q8, Q9, Q10, Q11]), "radius" : 1 * mm, "tangentPropagation" : true, "allowEdgeOverflow" : false});
        }
        {
            var Q0;
            {var subQ1=sQuery(id+"F11.wireOp",EDGE,"E77.right");Q0=makeQuery(id+"F11.imprint","IMPRINT",FACE,{"disambiguationData":[TD([[makeQuery(id+"F11.imprint","IMPRINT",EDGE,{"derivedFrom":subQ1}),-1.0]])]});}
            extrude(context, id + "F19", {"entities" : qUnion([Q0]), "operationType" : NewBodyOperationType.REMOVE, "oppositeDirection" : true, "depth" : 4 * mm, "offsetDistance" : 25 * mm});
        }
        {
            var Q0;
            Q0=makeQuery(id+"F19.boolean.opBoolean","COPY",FACE,{"derivedFrom":makeQuery(id+"F19.opExtrude","CAP_FACE",FACE,{"disambiguationData":[OSD([sQuery(id+"F11.wireOp",EDGE,"E73.0.0"),sQuery(id+"F11.wireOp",EDGE,"E73.0.2"),sQuery(id+"F11.wireOp",EDGE,"E77.right"),sQuery(id+"F11.wireOp",EDGE,"E84.MirrorCS"),sQuery(id+"F11.wireOp",EDGE,"E96"),sQuery(id+"F11.wireOp",EDGE,"E97"),sQuery(id+"F11.wireOp",EDGE,"E98.MirrorC"),sQuery(id+"F11.wireOp",EDGE,"E100.MirrorC")])],"isStart":false})});
            var sketch = newSketch(context, id + "F20", { "sketchPlane" : qUnion([Q0])});
            skLineSegment(sketch, "E118.0.0", {"start": v(-370, 1595) * mm, "end": v(370, 1595) * mm});
            skLineSegment(sketch, "E118.0.1", {"start": v(370, 1595) * mm, "end": v(370, 2035) * mm});
            skLineSegment(sketch, "E118.0.2", {"start": v(370, 2035) * mm, "end": v(-370, 2035) * mm});
            skLineSegment(sketch, "E118.0.3", {"start": v(-370, 2035) * mm, "end": v(-370, 1595) * mm});
            skLineSegment(sketch, "E119.bottom", {"start": v(-370, 2035) * mm, "end": v(370, 2035) * mm});
            skLineSegment(sketch, "E119.right", {"start": v(370, 2035) * mm, "end": v(370, 1595) * mm});
            skSolve(sketch);
        }
        {
            var Q0;
            Q0 = qSketchRegion(id + "F20", true);
            extrude(context, id + "F21", {"entities" : qUnion([Q0]), "depth" : 4 * mm, "offsetDistance" : 25 * mm});
        }
        {
            var Q0;
            Q0=makeQuery(id+"F2.opExtrude","SWEPT_FACE",FACE,{"disambiguationData":[OSD([sQuery(id+"F0.wireOp",EDGE,"E10.left")])]});
            var sketch = newSketch(context, id + "F22", { "sketchPlane" : qUnion([Q0])});
            skLineSegment(sketch, "E120.bottom", {"start": v(-1314, 0) * mm, "end": v(-1041, 0) * mm});
            skLineSegment(sketch, "E120.top", {"start": v(-1314, 250) * mm, "end": v(-1041, 250) * mm});
            skLineSegment(sketch, "E120.left", {"start": v(-1314, 0) * mm, "end": v(-1314, 250) * mm});
            skLineSegment(sketch, "E120.right", {"start": v(-1041, 0) * mm, "end": v(-1041, 250) * mm});
            skSolve(sketch);
        }
        {
            var Q0;
            Q0 = qSketchRegion(id + "F22", true);
            extrude(context, id + "F23", {"entities" : qUnion([Q0]), "operationType" : NewBodyOperationType.REMOVE, "oppositeDirection" : true, "depth" : 2300 * mm, "offsetDistance" : 25 * mm});
        }
        {
            var Q0;
            Q0=makeQuery(id+"F2.opExtrude","SWEPT_FACE",FACE,{"disambiguationData":[OSD([sQuery(id+"F0.wireOp",EDGE,"E0.left")])]});
            var sketch = newSketch(context, id + "F24", { "sketchPlane" : qUnion([Q0])});
            skLineSegment(sketch, "E121.bottom", {"start": v(-730, 0) * mm, "end": v(0, 0) * mm});
            skLineSegment(sketch, "E121.top", {"start": v(-730, 250) * mm, "end": v(0, 250) * mm});
            skLineSegment(sketch, "E121.left", {"start": v(-730, 0) * mm, "end": v(-730, 250) * mm});
            skLineSegment(sketch, "E121.right", {"start": v(0, 0) * mm, "end": v(0, 250) * mm});
            skSolve(sketch);
        }
        {
            var Q0;
            Q0 = qSketchRegion(id + "F24", true);
            extrude(context, id + "F25", {"entities" : qUnion([Q0]), "operationType" : NewBodyOperationType.REMOVE, "oppositeDirection" : true, "depth" : 500 * mm, "offsetDistance" : 25 * mm});
        }
        {
            var Q0;
            Q0=makeQuery(id+"F1.opExtrude","SWEPT_BODY",BODY,{"disambiguationData":[OSD([sQuery(id+"F0.wireOp",EDGE,"E0.bottom"),sQuery(id+"F0.wireOp",EDGE,"E0.top"),sQuery(id+"F0.wireOp",EDGE,"E0.left"),sQuery(id+"F0.wireOp",EDGE,"E0.right")])]});
            deleteBodies(context, id + "F26", {"entities" : qUnion([Q0])});
        }
    });
